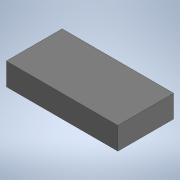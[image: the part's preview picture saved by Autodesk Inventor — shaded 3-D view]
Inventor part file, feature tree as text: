
AUTODESK INVENTOR PART (.ipt)
format: ipt  version: 2020 (Build 240168000, 168)  size: 102,912 bytes
history: native  units: in
note: dims shown in document units (in); Inventor stores cm internally (conversion verified against a paired STEP export)
features: extrude x1, sketch x1
ambient origin geometry x8: Origin, YZ Plane, XZ Plane, XY Plane, X Axis, Y Axis, Z Axis, Center Point
bodies: Solid1 (feature_tree)
feature tree (2):
  extrude  "Extrusion1"  Depth=0.5in
  sketch  "Sketch1"  dims[d0=1.0in d1=0.5in d2=0.2in d3=0.0in]
